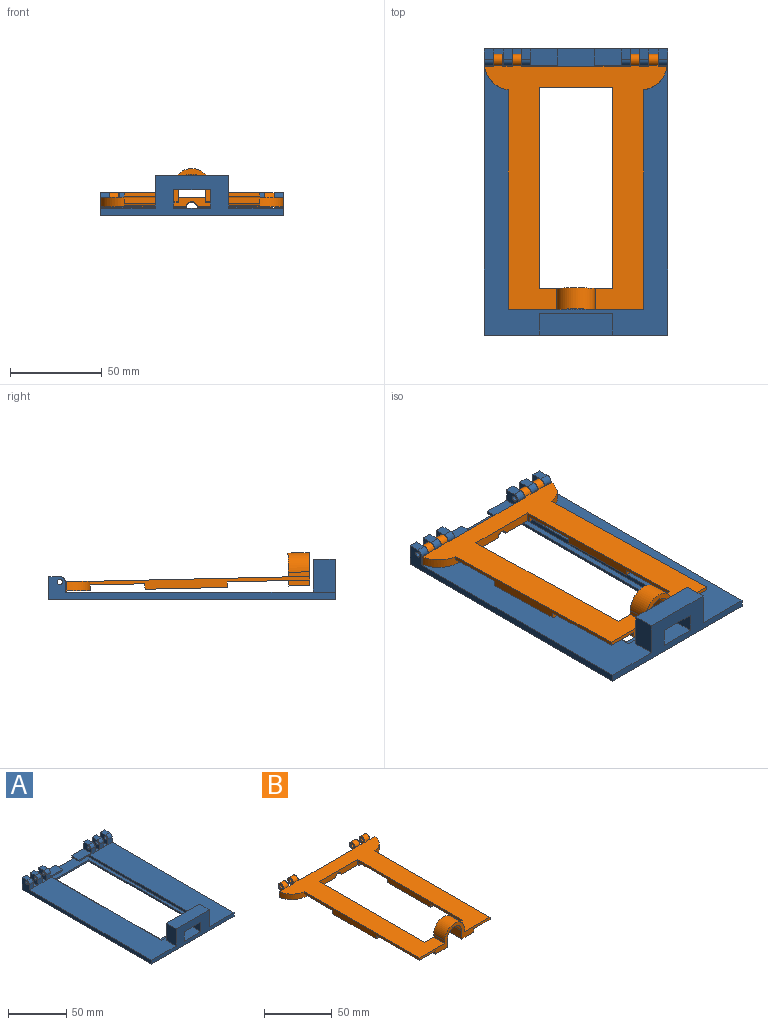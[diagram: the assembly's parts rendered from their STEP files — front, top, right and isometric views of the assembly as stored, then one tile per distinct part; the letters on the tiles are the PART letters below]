
ASSEMBLY  parts=2 mates=1
PART A: 69 faces, bbox 100x156.5x22 mm
  f0: plane 19.6x5.5mm, normal (0,-1,0), area 49.4mm2, adj f1,f18,f22,f48,f65,f66,f67
  f1: plane 13x9mm, normal (0,0,-1), area 117mm2, adj f0,f31,f34,f67
  f2: plane 14.6x9mm, normal (0,0,1), area 131.4mm2, adj f11,f34,f64,f68
  f3: plane 6x5mm, normal (0,0,1), area 30mm2, adj f18,f34,f48,f65
  f4: cylinder r=3mm len=5mm, axis (-1,0,0), area 23.6mm2, adj f11,f15,f45,f64
  f5: cylinder r=1.5mm len=5mm, axis (-1,0,0), area 47.1mm2, adj f45,f64
  f6: plane 156.5x100mm, normal (0,0,-1), area 10610mm2, adj f7,f23,f24,f25,f26,f27,f28,f34
  f7: plane 100x22mm, normal (0,-1,0), area 920mm2, adj f6,f22,f27,f28,f58,f59,f60,f61
  f8: plane 40x18mm, normal (0,1,0), area 520mm2, adj f22,f58,f59,f60,f61,f62,f63
  f9: plane 5.5x5mm, normal (0,-1,0), area 27.5mm2, adj f22,f27,f36,f53
  f10: plane 5.5x5mm, normal (0,-1,0), area 27.5mm2, adj f17,f22,f47,f52
  f11: plane 19.6x5.5mm, normal (0,-1,0), area 49.4mm2, adj f2,f4,f22,f33,f45,f64,f68
  f12: plane 5.5x5mm, normal (0,-1,0), area 27.5mm2, adj f19,f22,f41,f44
  f13: plane 6x5mm, normal (0,0,1), area 30mm2, adj f27,f34,f36,f53
  f14: plane 6x5mm, normal (0,0,1), area 30mm2, adj f17,f34,f47,f52
  f15: plane 6x5mm, normal (0,0,1), area 30mm2, adj f4,f34,f45,f64
  f16: plane 6x5mm, normal (0,0,1), area 30mm2, adj f19,f34,f41,f44
  f17: cylinder r=3mm len=5mm, axis (-1,0,0), area 23.6mm2, adj f10,f14,f47,f52
  f18: cylinder r=3mm len=5mm, axis (-1,0,0), area 23.6mm2, adj f0,f3,f48,f65
  f19: cylinder r=3mm len=5mm, axis (-1,0,0), area 23.6mm2, adj f12,f16,f41,f44
  f20: cylinder r=3mm len=5mm, axis (-1,0,0), area 23.6mm2, adj f28,f35,f37,f40
  f21: cylinder r=1.5mm len=5mm, axis (-1,0,0), area 47.1mm2, adj f28,f40
  f22: plane 147.5x100mm, normal (0,0,1), area 8415mm2, adj f0,f7,f8,f9,f10,f11,f12,f27
  f23: plane 126x1.5mm, normal (-1,0,0), area 189mm2, adj f6,f24,f26,f32
  f24: plane 40x1.5mm, normal (0,-1,0), area 60mm2, adj f6,f23,f25,f32
  f25: plane 126x1.5mm, normal (1,0,0), area 189mm2, adj f6,f24,f26,f32
  f26: plane 40x1.5mm, normal (0,1,0), area 60mm2, adj f6,f23,f25,f32
  f27: plane 156.5x12.5mm, normal (1,0,0), area 693.5mm2, adj f6,f7,f9,f13,f22,f34,f36,f38
  f28: plane 156.5x12.5mm, normal (-1,0,0), area 693.5mm2, adj f6,f7,f20,f21,f22,f34,f35,f37
  f29: plane 141.5x2.5mm, normal (1,0,0), area 353.7mm2, adj f22,f30,f32,f33,f34
  f30: plane 46x2.5mm, normal (0,1,0), area 115mm2, adj f22,f29,f31,f32
  f31: plane 141.5x2.5mm, normal (-1,0,0), area 353.7mm2, adj f1,f22,f30,f32,f34
  f32: plane 141.5x46mm, normal (0,0,1), area 1469mm2, adj f23,f24,f25,f26,f29,f30,f31,f34
  f33: plane 13x9mm, normal (0,0,-1), area 117mm2, adj f11,f29,f34,f68
  f34: plane 100x12.5mm, normal (0,1,0), area 573.4mm2, adj f1,f2,f3,f6,f13,f14,f15,f16
  f35: plane 5.5x5mm, normal (0,-1,0), area 27.5mm2, adj f20,f22,f28,f40
  f36: cylinder r=3mm len=5mm, axis (-1,0,0), area 23.6mm2, adj f9,f13,f27,f53
  f37: plane 6x5mm, normal (0,0,1), area 30mm2, adj f20,f28,f34,f40
  f38: cylinder r=1.5mm len=5mm, axis (-1,0,0), area 47.1mm2, adj f27,f53
  f39: plane 5.2x0.5mm, normal (0,1,0), area 2.6mm2, adj f22,f40,f41,f42
  f40: plane 9x9mm, normal (1,0,0), area 72mm2, adj f20,f21,f34,f35,f37,f39,f42
  f41: plane 9x9mm, normal (-1,0,0), area 72mm2, adj f12,f16,f19,f34,f39,f42,f56
  f42: plane 9x5.2mm, normal (0,0,1), area 46.8mm2, adj f34,f39,f40,f41
  f43: plane 5.2x0.5mm, normal (0,1,0), area 2.6mm2, adj f22,f44,f45,f46
  f44: plane 9x9mm, normal (1,0,0), area 72mm2, adj f12,f16,f19,f34,f43,f46,f56
  f45: plane 9x9mm, normal (-1,0,0), area 72mm2, adj f4,f5,f11,f15,f34,f43,f46
  f46: plane 9x5.2mm, normal (0,0,1), area 46.8mm2, adj f34,f43,f44,f45
  f47: plane 9x9mm, normal (-1,0,0), area 72mm2, adj f10,f14,f17,f34,f49,f50,f51
  f48: plane 9x9mm, normal (1,0,0), area 72mm2, adj f0,f3,f18,f34,f49,f50,f57
  f49: plane 5.2x0.5mm, normal (0,1,0), area 2.6mm2, adj f22,f47,f48,f50
  f50: plane 9x5.2mm, normal (0,0,1), area 46.8mm2, adj f34,f47,f48,f49
  f51: cylinder r=1.5mm len=5mm, axis (-1,0,0), area 47.1mm2, adj f47,f52
  f52: plane 9x9mm, normal (1,0,0), area 72mm2, adj f10,f14,f17,f34,f51,f54,f55
  f53: plane 9x9mm, normal (-1,0,0), area 72mm2, adj f9,f13,f34,f36,f38,f54,f55
  f54: plane 5.2x0.5mm, normal (0,1,0), area 2.6mm2, adj f22,f52,f53,f55
  f55: plane 9x5.2mm, normal (0,0,1), area 46.8mm2, adj f34,f52,f53,f54
  f56: cylinder r=1.5mm len=5mm, axis (-1,0,0), area 47.1mm2, adj f41,f44
  f57: cylinder r=1.5mm len=5mm, axis (-1,0,0), area 47.1mm2, adj f48,f65
  f58: plane 18x12mm, normal (-1,0,0), area 216mm2, adj f7,f8,f22,f60
  f59: plane 18x12mm, normal (1,0,0), area 216mm2, adj f7,f8,f22,f60
  f60: plane 40x12mm, normal (0,0,1), area 480mm2, adj f7,f8,f58,f59
  f61: plane 12x10mm, normal (1,0,0), area 120mm2, adj f7,f8,f22,f62
  f62: plane 20x12mm, normal (0,0,-1), area 240mm2, adj f7,f8,f61,f63
  f63: plane 12x10mm, normal (-1,0,0), area 120mm2, adj f7,f8,f22,f62
  f64: plane 9x7mm, normal (1,0,0), area 54mm2, adj f2,f4,f5,f11,f15,f34
  f65: plane 9x7mm, normal (-1,0,0), area 54mm2, adj f0,f3,f18,f34,f57,f66
  f66: plane 14.6x9mm, normal (0,0,1), area 131.4mm2, adj f0,f34,f65,f67
  f67: plane 9x1.5mm, normal (-1,0,0), area 13.5mm2, adj f0,f1,f34,f66
  f68: plane 9x1.5mm, normal (1,0,0), area 13.5mm2, adj f2,f11,f33,f34
PART B: 60 faces, bbox 99.7x139.5x18 mm
  f0: plane 12.5x11.5mm, normal (0,0,-1), area 143.8mm2, adj f1,f23,f35,f56
  f1: plane 74x18mm, normal (0,-1,0), area 292.8mm2, adj f0,f2,f16,f19,f20,f30,f32,f33
  f2: plane 133.5x99.73mm, normal (0,0,1), area 5452.3mm2, adj f1,f4,f5,f11,f12,f13,f14,f15
  f3: plane 46.89x13.5mm, normal (0,0,-1), area 542.6mm2, adj f4,f5,f9,f10,f21,f24,f36,f37
  f4: plane 40x5mm, normal (0,-1,0), area 188.1mm2, adj f2,f3,f6,f21,f22,f53
  f5: plane 59.4x5mm, normal (0,1,0), area 285.1mm2, adj f2,f3,f6,f44,f45,f53
  f6: plane 46.89x13.5mm, normal (0,0,-1), area 542.6mm2, adj f4,f5,f7,f8,f15,f22,f29,f39
  f7: plane 5x4.41mm, normal (0,0.47,-0.88), area 25mm2, adj f6,f11,f39,f47
  f8: plane 5x4.41mm, normal (0,0.47,-0.88), area 25mm2, adj f6,f12,f44,f48
  f9: plane 5x4.41mm, normal (0,0.47,-0.88), area 25mm2, adj f3,f13,f37,f43
  f10: plane 5x4.41mm, normal (0,0.47,-0.88), area 25mm2, adj f3,f14,f42,f45
  f11: cylinder r=3mm len=6mm, axis (-1,0,0), area 63.3mm2, adj f2,f7,f39,f47
  f12: cylinder r=3mm len=6mm, axis (-1,0,0), area 63.3mm2, adj f2,f8,f44,f48
  f13: cylinder r=3mm len=6mm, axis (-1,0,0), area 63.3mm2, adj f2,f9,f37,f43
  f14: cylinder r=3mm len=6mm, axis (-1,0,0), area 63.3mm2, adj f2,f10,f42,f45
  f15: cylinder r=15mm len=14.87mm, axis (0,0,-1), area 103.8mm2, adj f2,f6,f16,f28,f29,f40
  f16: plane 120.13x5mm, normal (1,0,0), area 375.3mm2, adj f1,f2,f15,f18,f27,f28,f33,f34
  f17: plane 45x17mm, normal (0,0,-1), area 765mm2, adj f20,f21,f25,f31
  f18: plane 45x17mm, normal (0,0,-1), area 765mm2, adj f16,f22,f27,f34
  f19: plane 12.5x11.5mm, normal (0,0,-1), area 143.7mm2, adj f1,f23,f32,f54
  f20: plane 120.13x5mm, normal (-1,0,0), area 375.3mm2, adj f1,f2,f17,f25,f26,f30,f31,f36
  f21: plane 110x5mm, normal (1,0,0), area 359.5mm2, adj f2,f3,f4,f17,f23,f24,f25,f26
  f22: plane 110x5mm, normal (-1,0,0), area 359.5mm2, adj f2,f4,f6,f18,f23,f27,f28,f29
  f23: plane 40x18mm, normal (0,1,0), area 224.8mm2, adj f0,f2,f19,f21,f22,f32,f35,f54
  f24: plane 15x3mm, normal (0,-1,0), area 45mm2, adj f3,f21,f26,f36
  f25: plane 17x3mm, normal (0,1,0), area 51mm2, adj f17,f20,f21,f26
  f26: plane 30.13x17mm, normal (0,0,-1), area 510.1mm2, adj f20,f21,f24,f25,f36
  f27: plane 17x3mm, normal (0,1,0), area 51mm2, adj f16,f18,f22,f28
  f28: plane 30.13x17mm, normal (0,0,-1), area 510.1mm2, adj f15,f16,f22,f27,f29
  f29: plane 15x3mm, normal (0,-1,0), area 45mm2, adj f6,f15,f22,f28
  f30: plane 45x17mm, normal (0,0,-1), area 765mm2, adj f1,f20,f21,f31,f32
  f31: plane 17x3mm, normal (0,-1,0), area 51mm2, adj f17,f20,f21,f30
  f32: plane 11.5x3mm, normal (-1,0,0), area 34.5mm2, adj f1,f19,f23,f30
  f33: plane 45x17mm, normal (0,0,-1), area 765mm2, adj f1,f16,f22,f34,f35
  f34: plane 17x3mm, normal (0,-1,0), area 51mm2, adj f16,f18,f22,f33
  f35: plane 11.5x3mm, normal (1,0,0), area 34.5mm2, adj f0,f1,f23,f33
  f36: cylinder r=15mm len=14.87mm, axis (0,0,1), area 103.8mm2, adj f2,f3,f20,f24,f26,f38
  f37: plane 8x6.5mm, normal (-1,0,0), area 29.4mm2, adj f2,f3,f9,f13,f38,f49
  f38: plane 5x4.97mm, normal (0,1,0), area 24.8mm2, adj f2,f3,f36,f37
  f39: plane 8x6.5mm, normal (1,0,0), area 29.4mm2, adj f2,f6,f7,f11,f40,f51
  f40: plane 5x4.97mm, normal (0,1,0), area 24.8mm2, adj f2,f6,f15,f39
  f41: plane 5.2x5mm, normal (0,1,0), area 26mm2, adj f2,f3,f42,f43
  f42: plane 8x6.5mm, normal (-1,0,0), area 29.4mm2, adj f2,f3,f10,f14,f41,f50
  f43: plane 8x6.5mm, normal (1,0,0), area 29.4mm2, adj f2,f3,f9,f13,f41,f49
  f44: plane 8x6.5mm, normal (-1,0,0), area 29.4mm2, adj f2,f5,f6,f8,f12,f52
  f45: plane 8x6.5mm, normal (1,0,0), area 29.4mm2, adj f2,f3,f5,f10,f14,f50
  f46: plane 5.2x5mm, normal (0,1,0), area 26mm2, adj f2,f6,f47,f48
  f47: plane 8x6.5mm, normal (-1,0,0), area 29.4mm2, adj f2,f6,f7,f11,f46,f51
  f48: plane 8x6.5mm, normal (1,0,0), area 29.4mm2, adj f2,f6,f8,f12,f46,f52
  f49: cylinder r=1.5mm len=5mm, axis (-1,0,0), area 47.1mm2, adj f37,f43
  f50: cylinder r=1.5mm len=5mm, axis (-1,0,0), area 47.1mm2, adj f42,f45
  f51: cylinder r=1.5mm len=5mm, axis (-1,0,0), area 47.1mm2, adj f39,f47
  f52: cylinder r=1.5mm len=5mm, axis (-1,0,0), area 47.1mm2, adj f44,f48
  f53: cylinder r=3mm len=11.5mm, axis (0,1,0), area 99.9mm2, adj f3,f4,f5,f6
  f54: plane 11.5x7.5mm, normal (1,0,0), area 86.2mm2, adj f1,f19,f23,f55
  f55: cylinder r=7.5mm len=15mm, axis (0,-1,0), area 271mm2, adj f1,f23,f54,f56
  f56: plane 11.5x7.5mm, normal (-1,0,0), area 86.2mm2, adj f0,f1,f23,f55
  f57: plane 11.5x2.5mm, normal (1,0,0), area 28.7mm2, adj f1,f2,f23,f58
  f58: cylinder r=10.5mm len=21mm, axis (0,-1,0), area 379.3mm2, adj f1,f23,f57,f59
  f59: plane 11.5x2.5mm, normal (-1,0,0), area 28.7mm2, adj f1,f2,f23,f58
PLACE A t=(-0.1,31.22,4.21)mm fixed
PLACE B rot(axis=(-1,0,0),1.3deg) t=(-0.2,30.45,-20.11)mm
MATE revolute B.f11 <-> A.f4  axis (-1,0,0) through (-45.1,99.22,13.71)mm
